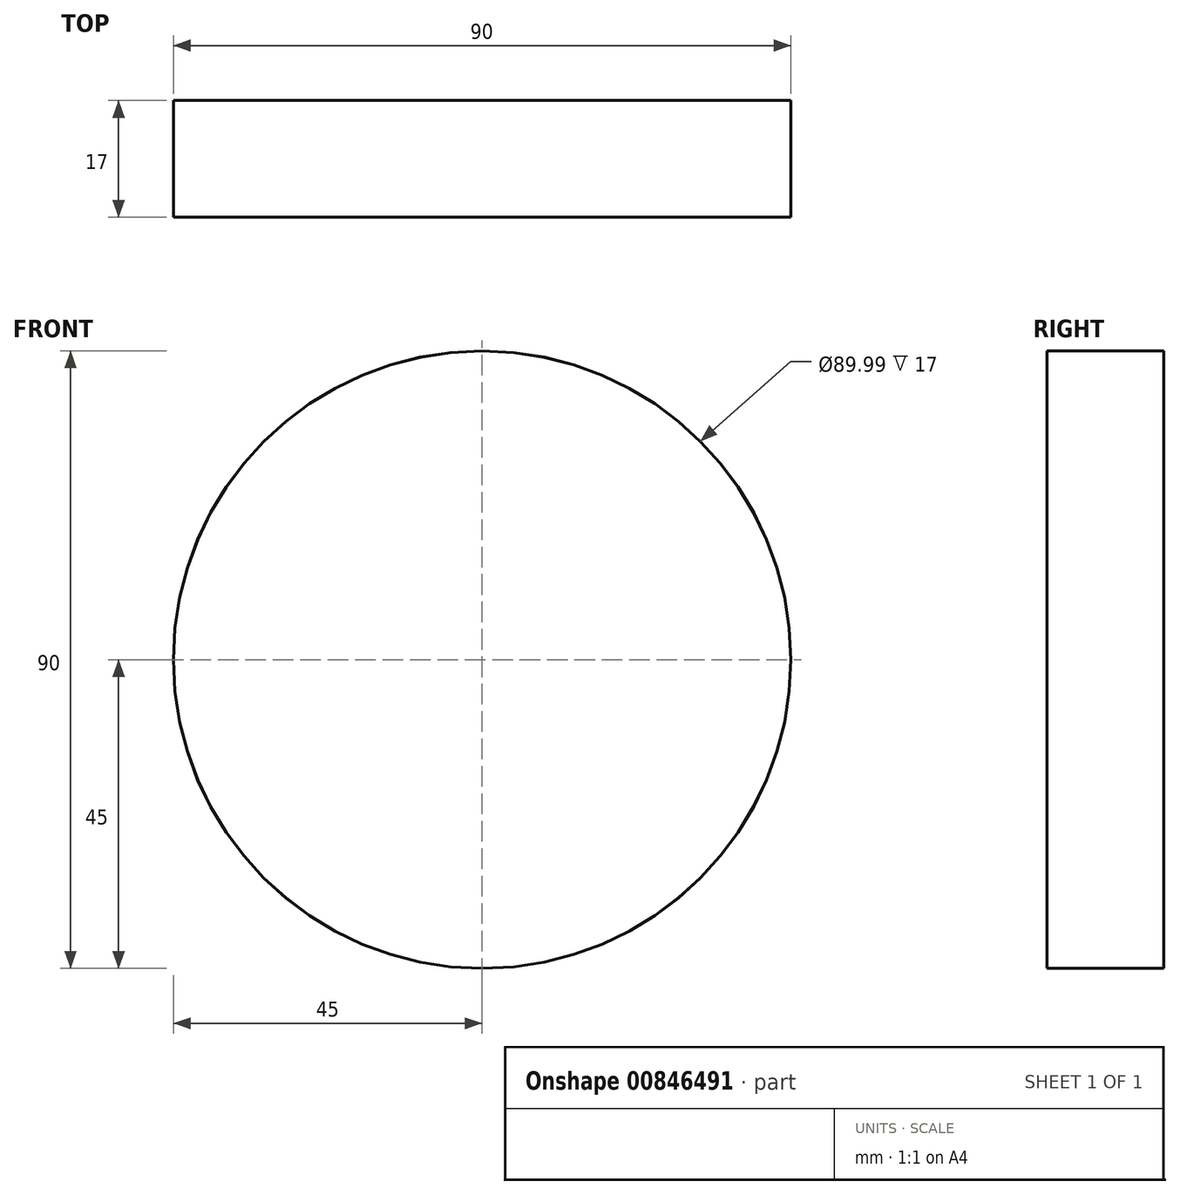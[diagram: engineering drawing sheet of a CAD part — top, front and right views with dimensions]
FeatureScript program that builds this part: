
annotation { "Feature Type Name" : "Feature", "Feature Type Description" : "" }
export const myFeature = defineFeature(function(context is Context, id is Id, definition is map)
    precondition{}
    {
        {
            var Q0;
            Q0=qCreatedBy(makeId("Front.planeOp"),FACE);
            var sketch = newSketch(context, id + "F0", { "sketchPlane" : qUnion([Q0])});
            skCircle(sketch, "E0", {"center": v(0, 0) * mm, "radius": 45 * mm});
            skSolve(sketch);
        }
        {
            var Q0;
            Q0 = qSketchRegion(id + "F0", true);
            extrude(context, id + "F1", {"entities" : qUnion([Q0]), "depth" : 17 * mm, "offsetDistance" : 25 * mm});
        }
    });
